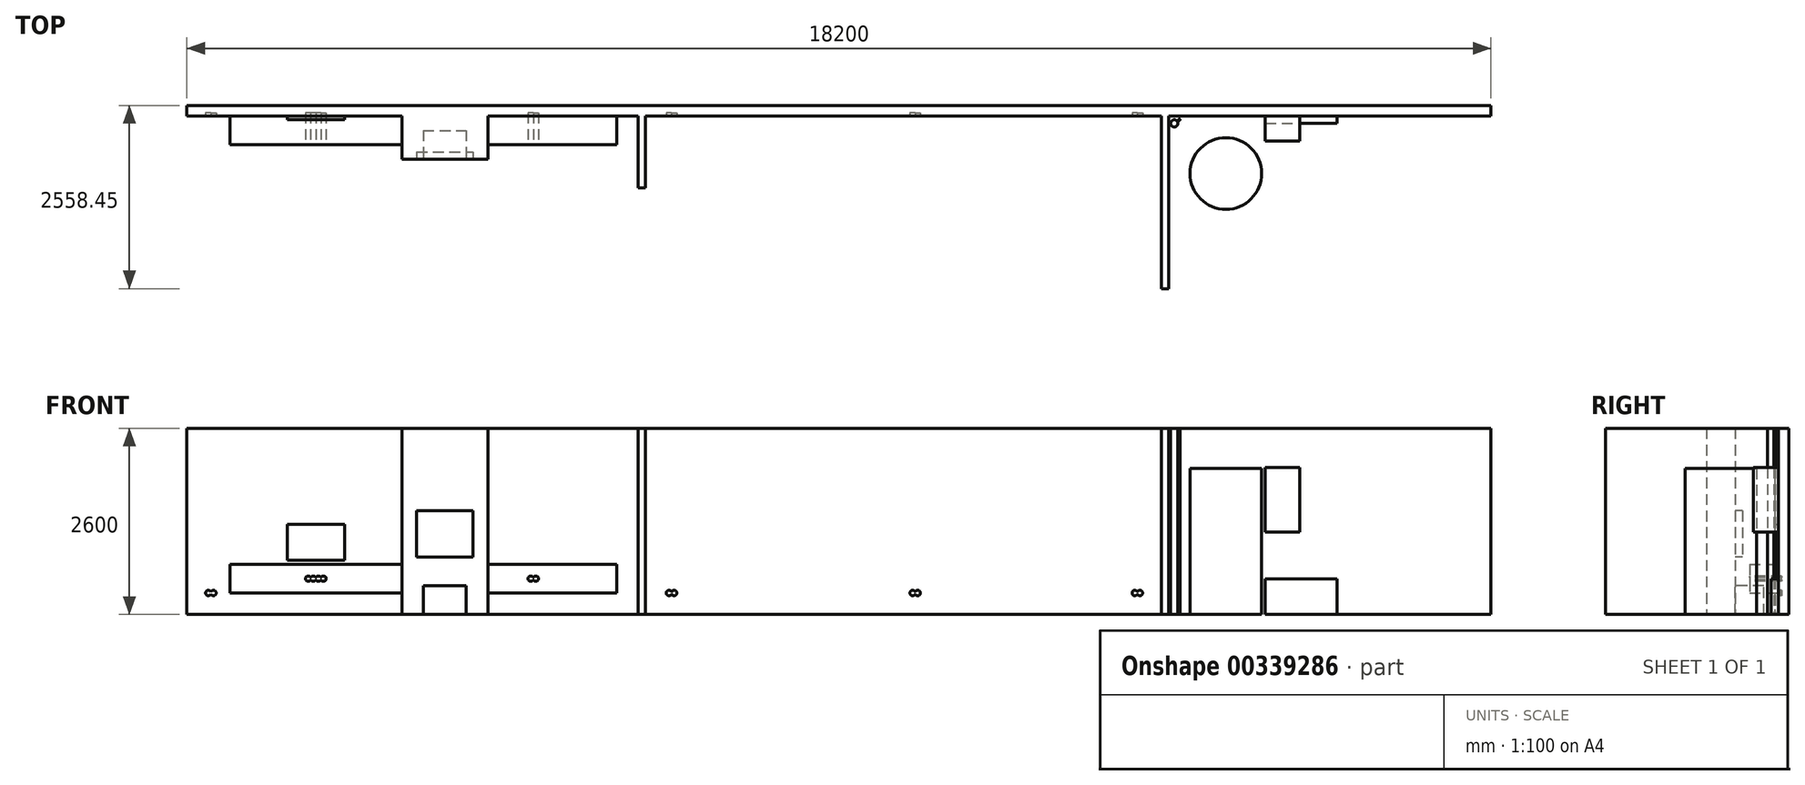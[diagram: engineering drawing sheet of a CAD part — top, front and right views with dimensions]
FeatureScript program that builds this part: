
annotation { "Feature Type Name" : "Feature", "Feature Type Description" : "" }
export const myFeature = defineFeature(function(context is Context, id is Id, definition is map)
    precondition{}
    {
        {
            var Q0;
            Q0=qCreatedBy(makeId("Top.planeOp"),FACE);
            var sketch = newSketch(context, id + "F0", { "sketchPlane" : qUnion([Q0])});
            skLineSegment(sketch, "E0.bottom", {"start": v(0, 0) * mm, "end": v(3000, 0) * mm});
            skLineSegment(sketch, "E0.top", {"start": v(0, 150) * mm, "end": v(18200, 150) * mm});
            skLineSegment(sketch, "E0.left", {"start": v(0, 150) * mm, "end": v(0, 0) * mm});
            skLineSegment(sketch, "E0.right", {"start": v(18200, 150) * mm, "end": v(18200, 0) * mm});
            skLineSegment(sketch, "E1.top", {"start": v(3000, -600) * mm, "end": v(4200, -600) * mm});
            skLineSegment(sketch, "E1.left", {"start": v(3000, 0) * mm, "end": v(3000, -600) * mm});
            skLineSegment(sketch, "E1.right", {"start": v(4200, 0) * mm, "end": v(4200, -600) * mm});
            skLineSegment(sketch, "E2.trimOffspring", {"start": v(4200, 0) * mm, "end": v(6300, 0) * mm});
            skLineSegment(sketch, "E3", {"start": v(13600, 0) * mm, "end": v(13600, -2408.45) * mm});
            skLineSegment(sketch, "E4", {"start": v(13600, -2408.45) * mm, "end": v(13700, -2408.45) * mm});
            skLineSegment(sketch, "E5", {"start": v(13700, -2408.45) * mm, "end": v(13700, 0) * mm});
            skLineSegment(sketch, "E6.trimOffspring", {"start": v(13700, 0) * mm, "end": v(18200, 0) * mm});
            skLineSegment(sketch, "E7", {"start": v(6300, 0) * mm, "end": v(6300, -1000) * mm});
            skLineSegment(sketch, "E8", {"start": v(6300, -1000) * mm, "end": v(6400, -1000) * mm});
            skLineSegment(sketch, "E9", {"start": v(6400, -1000) * mm, "end": v(6400, 0) * mm});
            skLineSegment(sketch, "E10.trimOffspring", {"start": v(6400, 0) * mm, "end": v(13600, 0) * mm});
            skCircle(sketch, "E11", {"center": v(14500, -800) * mm, "radius": 500 * mm});
            skCircle(sketch, "E12", {"center": v(13780, -100) * mm, "radius": 50 * mm});
            skCircle(sketch, "E13", {"center": v(13744, -250) * mm, "radius": 14 * mm});
            skCircle(sketch, "E14", {"center": v(13744, -310) * mm, "radius": 14 * mm});
            skCircle(sketch, "E15", {"center": v(13737.5, -400) * mm, "radius": 7.5 * mm});
            skCircle(sketch, "E16", {"center": v(13850, -50) * mm, "radius": 11 * mm});
            skSolve(sketch);
        }
        {
            var Q0;
            Q0=makeQuery(id+"F0.imprint","IMPRINT",FACE,{"disambiguationData":[TD([[makeQuery(id+"F0.imprint","IMPRINT",EDGE,{"derivedFrom":sQuery(id+"F0.wireOp",EDGE,"E0.bottom")}),1.0]])]});
            var Q1;
            Q1=makeQuery(id+"F0.imprint","IMPRINT",FACE,{"disambiguationData":[TD([[makeQuery(id+"F0.imprint","IMPRINT",EDGE,{"derivedFrom":sQuery(id+"F0.wireOp",EDGE,"E12")}),1.0]])]});
            var Q2;
            Q2=makeQuery(id+"F0.imprint","IMPRINT",FACE,{"disambiguationData":[TD([[makeQuery(id+"F0.imprint","IMPRINT",EDGE,{"derivedFrom":sQuery(id+"F0.wireOp",EDGE,"E16")}),1.0]])]});
            extrude(context, id + "F1", {"entities" : qUnion([Q0, Q1, Q2]), "depth" : 2600 * mm});
        }
        {
            var Q0;
            Q0=makeQuery(id+"F1.opExtrude","SWEPT_FACE",FACE,{"disambiguationData":[OSD([sQuery(id+"F0.wireOp",EDGE,"E1.top")])]});
            var sketch = newSketch(context, id + "F2", { "sketchPlane" : qUnion([Q0])});
            skLineSegment(sketch, "E17.bottom", {"start": v(3205, 1447) * mm, "end": v(3995, 1447) * mm});
            skLineSegment(sketch, "E17.top", {"start": v(3205, 800) * mm, "end": v(3995, 800) * mm});
            skLineSegment(sketch, "E17.left", {"start": v(3205, 1447) * mm, "end": v(3205, 800) * mm});
            skLineSegment(sketch, "E17.right", {"start": v(3995, 1447) * mm, "end": v(3995, 800) * mm});
            skLineSegment(sketch, "E18", {"start": v(3600, 0) * mm, "end": v(3600, 2600) * mm, "construction": true});
            skSolve(sketch);
        }
        {
            var Q0;
            Q0=makeQuery(id+"F2.imprint","IMPRINT",FACE,{"disambiguationData":[TD([[makeQuery(id+"F2.imprint","IMPRINT",EDGE,{"derivedFrom":sQuery(id+"F2.wireOp",EDGE,"E17.bottom")}),-1.0]])]});
            extrude(context, id + "F3", {"entities" : qUnion([Q0]), "operationType" : NewBodyOperationType.REMOVE, "oppositeDirection" : true, "depth" : 100 * mm});
        }
        {
            var Q0;
            Q0=makeQuery(id+"F1.opExtrude","SWEPT_FACE",FACE,{"disambiguationData":[OSD([sQuery(id+"F0.wireOp",EDGE,"E0.bottom")])]});
            var sketch = newSketch(context, id + "F4", { "sketchPlane" : qUnion([Q0])});
            skLineSegment(sketch, "E19.bottom", {"start": v(3000, 700) * mm, "end": v(600, 700) * mm});
            skLineSegment(sketch, "E19.top", {"start": v(3000, 300) * mm, "end": v(600, 300) * mm});
            skLineSegment(sketch, "E19.left", {"start": v(3000, 700) * mm, "end": v(3000, 300) * mm});
            skLineSegment(sketch, "E19.right", {"start": v(600, 700) * mm, "end": v(600, 300) * mm});
            skLineSegment(sketch, "E20.0", {"start": v(4200, 2600) * mm, "end": v(4200, 0) * mm, "construction": true});
            skLineSegment(sketch, "E21.bottom", {"start": v(4200, 700) * mm, "end": v(6000, 700) * mm});
            skLineSegment(sketch, "E21.top", {"start": v(4200, 300) * mm, "end": v(6000, 300) * mm});
            skLineSegment(sketch, "E21.left", {"start": v(4200, 700) * mm, "end": v(4200, 300) * mm});
            skLineSegment(sketch, "E21.right", {"start": v(6000, 700) * mm, "end": v(6000, 300) * mm});
            skSolve(sketch);
        }
        {
            var Q0;
            Q0 = qSketchRegion(id + "F4", true);
            extrude(context, id + "F5", {"entities" : qUnion([Q0]), "operationType" : NewBodyOperationType.ADD, "depth" : 400 * mm});
        }
        {
            var Q0;
            Q0=makeQuery(id+"F1.opExtrude","SWEPT_FACE",FACE,{"disambiguationData":[OSD([sQuery(id+"F0.wireOp",EDGE,"E0.bottom")])]});
            var sketch = newSketch(context, id + "F6", { "sketchPlane" : qUnion([Q0])});
            skLineSegment(sketch, "E22.bottom", {"start": v(1400, 1260) * mm, "end": v(2200, 1260) * mm});
            skLineSegment(sketch, "E22.top", {"start": v(1400, 760) * mm, "end": v(2200, 760) * mm});
            skLineSegment(sketch, "E22.left", {"start": v(1400, 1260) * mm, "end": v(1400, 760) * mm});
            skLineSegment(sketch, "E22.right", {"start": v(2200, 1260) * mm, "end": v(2200, 760) * mm});
            skSolve(sketch);
        }
        {
            var Q0;
            Q0=makeQuery(id+"F6.imprint","IMPRINT",FACE,{"disambiguationData":[TD([[makeQuery(id+"F6.imprint","IMPRINT",EDGE,{"derivedFrom":sQuery(id+"F6.wireOp",EDGE,"E22.bottom")}),-1.0]])]});
            extrude(context, id + "F7", {"entities" : qUnion([Q0]), "operationType" : NewBodyOperationType.ADD, "depth" : 50 * mm});
        }
        {
            var Q0;
            Q0=makeQuery(id+"F1.opExtrude","SWEPT_FACE",FACE,{"disambiguationData":[OSD([sQuery(id+"F0.wireOp",EDGE,"E10.trimOffspring")])]});
            var sketch = newSketch(context, id + "F8", { "sketchPlane" : qUnion([Q0])});
            skArc(sketch, "E23", {"start": v(13264.5, 286.44) * mm, "mid": v(13338, 300) * mm, "end": v(13264.5, 313.56) * mm});
            skArc(sketch, "E24", {"start": v(13264.5, 313.56) * mm, "mid": v(13191, 300) * mm, "end": v(13264.5, 286.44) * mm});
            skArc(sketch, "E25", {"start": v(10164.5, 286.44) * mm, "mid": v(10238, 300) * mm, "end": v(10164.5, 313.56) * mm});
            skArc(sketch, "E26", {"start": v(10164.5, 313.56) * mm, "mid": v(10091, 300) * mm, "end": v(10164.5, 286.44) * mm});
            skArc(sketch, "E27", {"start": v(6764.5, 286.44) * mm, "mid": v(6838, 300) * mm, "end": v(6764.5, 313.56) * mm});
            skArc(sketch, "E28", {"start": v(6764.5, 313.56) * mm, "mid": v(6691, 300) * mm, "end": v(6764.5, 286.44) * mm});
            skArc(sketch, "E29", {"start": v(4835.5, 486.44) * mm, "mid": v(4909, 500) * mm, "end": v(4835.5, 513.56) * mm});
            skArc(sketch, "E30", {"start": v(4835.5, 513.56) * mm, "mid": v(4762, 500) * mm, "end": v(4835.5, 486.44) * mm});
            skArc(sketch, "E31", {"start": v(335.5, 286.44) * mm, "mid": v(409, 300) * mm, "end": v(335.5, 313.56) * mm});
            skArc(sketch, "E32", {"start": v(335.5, 313.56) * mm, "mid": v(262, 300) * mm, "end": v(335.5, 286.44) * mm});
            skArc(sketch, "E33", {"start": v(1871, 486.44) * mm, "mid": v(1944.5, 500) * mm, "end": v(1871, 513.56) * mm});
            skArc(sketch, "E34", {"start": v(1871, 513.56) * mm, "mid": v(1835.5, 538) * mm, "end": v(1800, 513.56) * mm});
            skArc(sketch, "E35", {"start": v(1729, 486.44) * mm, "mid": v(1764.5, 462) * mm, "end": v(1800, 486.44) * mm});
            skArc(sketch, "E36", {"start": v(1729, 513.56) * mm, "mid": v(1655.5, 500) * mm, "end": v(1729, 486.44) * mm});
            skArc(sketch, "E37.trimOffspring", {"start": v(1800, 486.44) * mm, "mid": v(1835.5, 462) * mm, "end": v(1871, 486.44) * mm});
            skArc(sketch, "E38.trimOffspring", {"start": v(1800, 513.56) * mm, "mid": v(1764.5, 538) * mm, "end": v(1729, 513.56) * mm});
            skSolve(sketch);
        }
        {
            var Q0;
            Q0 = qSketchRegion(id + "F8", true);
            var Q1;
            Q1=makeQuery(id+"F1.opExtrude","SWEPT_FACE",FACE,{"disambiguationData":[OSD([sQuery(id+"F0.wireOp",EDGE,"E1.top")])]});
            extrude(context, id + "F9", {"entities" : qUnion([Q0]), "operationType" : NewBodyOperationType.REMOVE, "oppositeDirection" : true, "depth" : 50 * mm, "hasSecondDirection" : true, "secondDirectionBound" : SecondDirectionBoundingType.UP_TO_SURFACE, "secondDirectionOppositeDirection" : false, "secondDirectionBoundEntityFace" : qUnion([Q1]), "secondDirectionDepth" : 400 * mm});
        }
        {
            var Q0;
            Q0=makeQuery(id+"F0.imprint","IMPRINT",FACE,{"disambiguationData":[TD([[makeQuery(id+"F0.imprint","IMPRINT",EDGE,{"derivedFrom":sQuery(id+"F0.wireOp",EDGE,"E11")}),1.0]])]});
            extrude(context, id + "F10", {"entities" : qUnion([Q0]), "depth" : 2040 * mm});
        }
        {
            var Q0;
            Q0=makeQuery(id+"F1.opExtrude","SWEPT_FACE",FACE,{"disambiguationData":[OSD([sQuery(id+"F0.wireOp",EDGE,"E6.trimOffspring")])]});
            var sketch = newSketch(context, id + "F11", { "sketchPlane" : qUnion([Q0])});
            skLineSegment(sketch, "E39.bottom", {"start": v(15050, 0) * mm, "end": v(16050, 0) * mm});
            skLineSegment(sketch, "E39.top", {"start": v(15050, 500) * mm, "end": v(16050, 500) * mm});
            skLineSegment(sketch, "E39.left", {"start": v(15050, 0) * mm, "end": v(15050, 500) * mm});
            skLineSegment(sketch, "E39.right", {"start": v(16050, 0) * mm, "end": v(16050, 500) * mm});
            skSolve(sketch);
        }
        {
            var Q0;
            Q0=makeQuery(id+"F11.imprint","IMPRINT",FACE,{"disambiguationData":[TD([[makeQuery(id+"F11.imprint","IMPRINT",EDGE,{"derivedFrom":sQuery(id+"F11.wireOp",EDGE,"E39.bottom")}),1.0]])]});
            extrude(context, id + "F12", {"entities" : qUnion([Q0]), "operationType" : NewBodyOperationType.ADD, "depth" : 100 * mm});
        }
        {
            var Q0;
            Q0=makeQuery(id+"F1.opExtrude","SWEPT_FACE",FACE,{"disambiguationData":[OSD([sQuery(id+"F0.wireOp",EDGE,"E1.top")])]});
            var sketch = newSketch(context, id + "F13", { "sketchPlane" : qUnion([Q0])});
            skLineSegment(sketch, "E40.bottom", {"start": v(3300, 0) * mm, "end": v(3900, 0) * mm});
            skLineSegment(sketch, "E40.top", {"start": v(3300, 400) * mm, "end": v(3900, 400) * mm});
            skLineSegment(sketch, "E40.left", {"start": v(3300, 0) * mm, "end": v(3300, 400) * mm});
            skLineSegment(sketch, "E40.right", {"start": v(3900, 0) * mm, "end": v(3900, 400) * mm});
            skSolve(sketch);
        }
        {
            var Q0;
            Q0=makeQuery(id+"F13.imprint","IMPRINT",FACE,{"disambiguationData":[TD([[makeQuery(id+"F13.imprint","IMPRINT",EDGE,{"derivedFrom":sQuery(id+"F13.wireOp",EDGE,"E40.bottom")}),1.0]])]});
            extrude(context, id + "F14", {"entities" : qUnion([Q0]), "operationType" : NewBodyOperationType.REMOVE, "oppositeDirection" : true, "depth" : 400 * mm});
        }
        {
            var Q0;
            Q0=makeQuery(id+"F11.imprint","IMPRINT",FACE,{"disambiguationData":[TD([[makeQuery(id+"F11.imprint","IMPRINT",EDGE,{"derivedFrom":sQuery(id+"F11.wireOp",EDGE,"E39.top")}),1.0]])]});
            var sketch = newSketch(context, id + "F15", { "sketchPlane" : qUnion([Q0])});
            skLineSegment(sketch, "E41.bottom", {"start": v(15050, 2050) * mm, "end": v(15530, 2050) * mm});
            skLineSegment(sketch, "E41.top", {"start": v(15050, 1150) * mm, "end": v(15530, 1150) * mm});
            skLineSegment(sketch, "E41.left", {"start": v(15050, 2050) * mm, "end": v(15050, 1150) * mm});
            skLineSegment(sketch, "E41.right", {"start": v(15530, 2050) * mm, "end": v(15530, 1150) * mm});
            skSolve(sketch);
        }
        {
            var Q0;
            Q0=makeQuery(id+"F15.imprint","IMPRINT",FACE,{"disambiguationData":[TD([[makeQuery(id+"F15.imprint","IMPRINT",EDGE,{"derivedFrom":sQuery(id+"F15.wireOp",EDGE,"E41.bottom")}),-1.0]])]});
            extrude(context, id + "F16", {"entities" : qUnion([Q0]), "operationType" : NewBodyOperationType.ADD, "depth" : 344 * mm});
        }
    });
